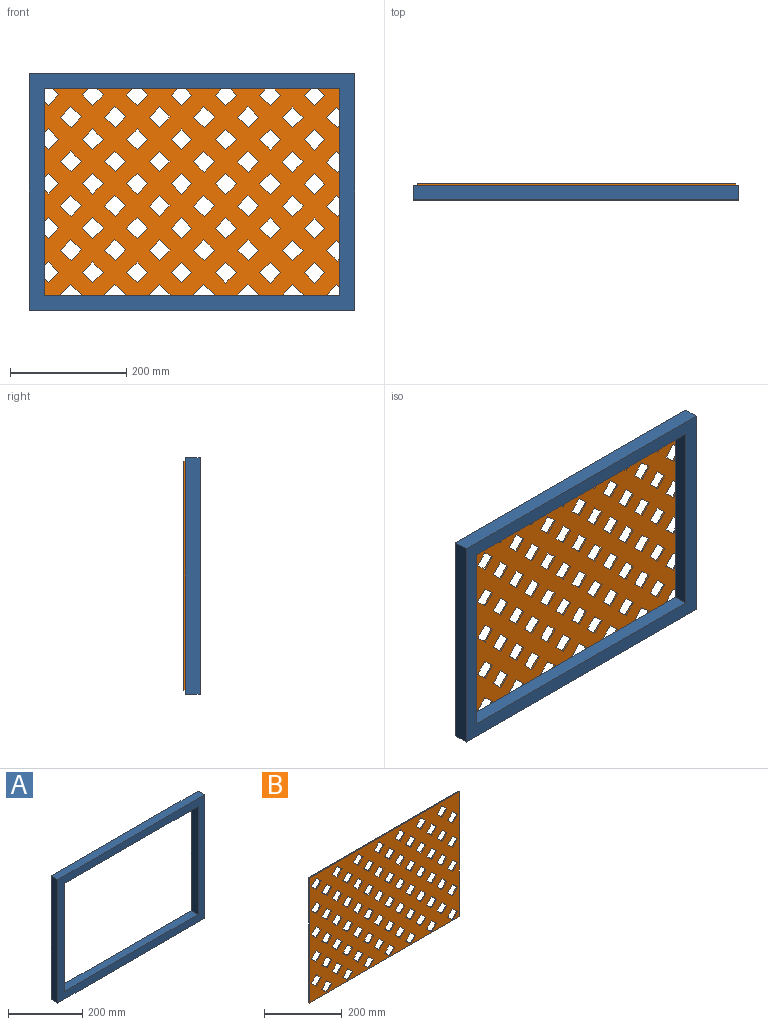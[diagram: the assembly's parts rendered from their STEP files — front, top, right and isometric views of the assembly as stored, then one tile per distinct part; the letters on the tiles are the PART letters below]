
ASSEMBLY  parts=2 mates=1
PART A: 10 faces, bbox 558.8x25.4x406.4 mm
  f0: plane 558.8x406.4mm, normal (0,-1,0), area 46451.5mm2, adj f2,f3,f4,f5,f6,f7,f8,f9
  f1: plane 558.8x406.4mm, normal (0,1,0), area 46451.5mm2, adj f2,f3,f4,f5,f6,f7,f8,f9
  f2: plane 558.8x25.4mm, normal (0,0,-1), area 14193.5mm2, adj f0,f1,f3,f5
  f3: plane 406.4x25.4mm, normal (1,0,0), area 10322.6mm2, adj f0,f1,f2,f4
  f4: plane 558.8x25.4mm, normal (0,0,1), area 14193.5mm2, adj f0,f1,f3,f5
  f5: plane 406.4x25.4mm, normal (-1,0,0), area 10322.6mm2, adj f0,f1,f2,f4
  f6: plane 508x25.4mm, normal (0,0,1), area 12903.2mm2, adj f0,f1,f7,f9
  f7: plane 355.6x25.4mm, normal (-1,0,0), area 9032.2mm2, adj f0,f1,f6,f8
  f8: plane 508x25.4mm, normal (0,0,-1), area 12903.2mm2, adj f0,f1,f7,f9
  f9: plane 355.6x25.4mm, normal (1,0,0), area 9032.2mm2, adj f0,f1,f6,f8
PART B: 286 faces, bbox 546.1x2.5x393.7 mm
  f0: plane 546.1x393.7mm, normal (0,-1,0), area 169838.4mm2, adj f2,f3,f4,f5,f6,f7,f8,f9
  f1: plane 546.1x393.7mm, normal (0,1,0), area 169838.4mm2, adj f2,f3,f4,f5,f6,f7,f8,f9
  f2: plane 546.1x2.54mm, normal (0,0,-1), area 1387.1mm2, adj f0,f1,f3,f5
  f3: plane 393.7x2.54mm, normal (1,0,0), area 1000mm2, adj f0,f1,f2,f4
  f4: plane 546.1x2.54mm, normal (0,0,1), area 1387.1mm2, adj f0,f1,f3,f5
  f5: plane 393.7x2.54mm, normal (-1,0,0), area 1000mm2, adj f0,f1,f2,f4
  f6: plane 17.96x17.96mm, normal (-0.71,0,-0.71), area 64.5mm2, adj f0,f1,f7,f8
  f7: plane 17.96x17.96mm, normal (-0.71,0,0.71), area 64.5mm2, adj f0,f1,f6,f9
  f8: plane 17.96x17.96mm, normal (0.71,0,-0.71), area 64.5mm2, adj f0,f1,f6,f9
  f9: plane 17.96x17.96mm, normal (0.71,0,0.71), area 64.5mm2, adj f0,f1,f7,f8
  f10: plane 17.96x17.96mm, normal (-0.71,0,-0.71), area 64.5mm2, adj f0,f1,f11,f12
  f11: plane 17.96x17.96mm, normal (-0.71,0,0.71), area 64.5mm2, adj f0,f1,f10,f13
  f12: plane 17.96x17.96mm, normal (0.71,0,-0.71), area 64.5mm2, adj f0,f1,f10,f13
  f13: plane 17.96x17.96mm, normal (0.71,0,0.71), area 64.5mm2, adj f0,f1,f11,f12
  f14: plane 18.43x17.48mm, normal (-0.69,0,-0.73), area 64.5mm2, adj f0,f1,f15,f16
  f15: plane 18.43x17.48mm, normal (-0.73,0,0.69), area 64.5mm2, adj f0,f1,f14,f17
  f16: plane 18.43x17.48mm, normal (0.73,0,-0.69), area 64.5mm2, adj f0,f1,f14,f17
  f17: plane 18.43x17.48mm, normal (0.69,0,0.73), area 64.5mm2, adj f0,f1,f15,f16
  f18: plane 18.43x17.48mm, normal (-0.69,0,-0.73), area 64.5mm2, adj f0,f1,f19,f20
  f19: plane 18.43x17.48mm, normal (-0.73,0,0.69), area 64.5mm2, adj f0,f1,f18,f21
  f20: plane 18.43x17.48mm, normal (0.73,0,-0.69), area 64.5mm2, adj f0,f1,f18,f21
  f21: plane 18.43x17.48mm, normal (0.69,0,0.73), area 64.5mm2, adj f0,f1,f19,f20
  f22: plane 17.96x17.96mm, normal (0.71,0,-0.71), area 64.5mm2, adj f0,f1,f23,f24
  f23: plane 17.96x17.96mm, normal (-0.71,0,-0.71), area 64.5mm2, adj f0,f1,f22,f25
  f24: plane 17.96x17.96mm, normal (0.71,0,0.71), area 64.5mm2, adj f0,f1,f22,f25
  f25: plane 17.96x17.96mm, normal (-0.71,0,0.71), area 64.5mm2, adj f0,f1,f23,f24
  f26: plane 18.43x17.48mm, normal (-0.69,0,-0.73), area 64.5mm2, adj f0,f1,f27,f28
  f27: plane 18.43x17.48mm, normal (-0.73,0,0.69), area 64.5mm2, adj f0,f1,f26,f29
  f28: plane 18.43x17.48mm, normal (0.73,0,-0.69), area 64.5mm2, adj f0,f1,f26,f29
  f29: plane 18.43x17.48mm, normal (0.69,0,0.73), area 64.5mm2, adj f0,f1,f27,f28
  f30: plane 17.96x17.96mm, normal (0.71,0,0.71), area 64.5mm2, adj f0,f1,f31,f33
  f31: plane 17.96x17.96mm, normal (-0.71,0,0.71), area 64.5mm2, adj f0,f1,f30,f32
  f32: plane 17.96x17.96mm, normal (-0.71,0,-0.71), area 64.5mm2, adj f0,f1,f31,f33
  f33: plane 17.96x17.96mm, normal (0.71,0,-0.71), area 64.5mm2, adj f0,f1,f30,f32
  f34: plane 17.96x17.96mm, normal (0.71,0,-0.71), area 64.5mm2, adj f0,f1,f35,f36
  f35: plane 17.96x17.96mm, normal (-0.71,0,-0.71), area 64.5mm2, adj f0,f1,f34,f37
  f36: plane 17.96x17.96mm, normal (0.71,0,0.71), area 64.5mm2, adj f0,f1,f34,f37
  f37: plane 17.96x17.96mm, normal (-0.71,0,0.71), area 64.5mm2, adj f0,f1,f35,f36
  f38: plane 17.96x17.96mm, normal (-0.71,0,-0.71), area 64.5mm2, adj f0,f1,f39,f40
  f39: plane 17.96x17.96mm, normal (-0.71,0,0.71), area 64.5mm2, adj f0,f1,f38,f41
  f40: plane 17.96x17.96mm, normal (0.71,0,-0.71), area 64.5mm2, adj f0,f1,f38,f41
  f41: plane 17.96x17.96mm, normal (0.71,0,0.71), area 64.5mm2, adj f0,f1,f39,f40
  f42: plane 18.43x17.48mm, normal (0.73,0,-0.69), area 64.5mm2, adj f0,f1,f43,f44
  f43: plane 18.43x17.48mm, normal (-0.69,0,-0.73), area 64.5mm2, adj f0,f1,f42,f45
  f44: plane 18.43x17.48mm, normal (0.69,0,0.73), area 64.5mm2, adj f0,f1,f42,f45
  f45: plane 18.43x17.48mm, normal (-0.73,0,0.69), area 64.5mm2, adj f0,f1,f43,f44
  f46: plane 18.43x17.48mm, normal (0.73,0,-0.69), area 64.5mm2, adj f0,f1,f47,f48
  f47: plane 18.43x17.48mm, normal (-0.69,0,-0.73), area 64.5mm2, adj f0,f1,f46,f49
  f48: plane 18.43x17.48mm, normal (0.69,0,0.73), area 64.5mm2, adj f0,f1,f46,f49
  f49: plane 18.43x17.48mm, normal (-0.73,0,0.69), area 64.5mm2, adj f0,f1,f47,f48
  f50: plane 18.43x17.48mm, normal (-0.69,0,-0.73), area 64.5mm2, adj f0,f1,f51,f52
  f51: plane 18.43x17.48mm, normal (-0.73,0,0.69), area 64.5mm2, adj f0,f1,f50,f53
  f52: plane 18.43x17.48mm, normal (0.73,0,-0.69), area 64.5mm2, adj f0,f1,f50,f53
  f53: plane 18.43x17.48mm, normal (0.69,0,0.73), area 64.5mm2, adj f0,f1,f51,f52
  f54: plane 17.96x17.96mm, normal (-0.71,0,-0.71), area 64.5mm2, adj f0,f1,f55,f56
  f55: plane 17.96x17.96mm, normal (-0.71,0,0.71), area 64.5mm2, adj f0,f1,f54,f57
  f56: plane 17.96x17.96mm, normal (0.71,0,-0.71), area 64.5mm2, adj f0,f1,f54,f57
  f57: plane 17.96x17.96mm, normal (0.71,0,0.71), area 64.5mm2, adj f0,f1,f55,f56
  f58: plane 18.43x17.48mm, normal (-0.69,0,-0.73), area 64.5mm2, adj f0,f1,f59,f60
  f59: plane 18.43x17.48mm, normal (-0.73,0,0.69), area 64.5mm2, adj f0,f1,f58,f61
  f60: plane 18.43x17.48mm, normal (0.73,0,-0.69), area 64.5mm2, adj f0,f1,f58,f61
  f61: plane 18.43x17.48mm, normal (0.69,0,0.73), area 64.5mm2, adj f0,f1,f59,f60
  f62: plane 18.43x17.48mm, normal (-0.69,0,-0.73), area 64.5mm2, adj f0,f1,f63,f64
  f63: plane 18.43x17.48mm, normal (-0.73,0,0.69), area 64.5mm2, adj f0,f1,f62,f65
  f64: plane 18.43x17.48mm, normal (0.73,0,-0.69), area 64.5mm2, adj f0,f1,f62,f65
  f65: plane 18.43x17.48mm, normal (0.69,0,0.73), area 64.5mm2, adj f0,f1,f63,f64
  f66: plane 18.43x17.48mm, normal (0.73,0,-0.69), area 64.5mm2, adj f0,f1,f67,f68
  f67: plane 18.43x17.48mm, normal (-0.69,0,-0.73), area 64.5mm2, adj f0,f1,f66,f69
  f68: plane 18.43x17.48mm, normal (0.69,0,0.73), area 64.5mm2, adj f0,f1,f66,f69
  f69: plane 18.43x17.48mm, normal (-0.73,0,0.69), area 64.5mm2, adj f0,f1,f67,f68
  f70: plane 17.96x17.96mm, normal (0.71,0,0.71), area 64.5mm2, adj f0,f1,f71,f73
  f71: plane 17.96x17.96mm, normal (-0.71,0,0.71), area 64.5mm2, adj f0,f1,f70,f72
  f72: plane 17.96x17.96mm, normal (-0.71,0,-0.71), area 64.5mm2, adj f0,f1,f71,f73
  f73: plane 17.96x17.96mm, normal (0.71,0,-0.71), area 64.5mm2, adj f0,f1,f70,f72
  f74: plane 17.96x17.96mm, normal (0.71,0,-0.71), area 64.5mm2, adj f0,f1,f75,f76
  f75: plane 17.96x17.96mm, normal (-0.71,0,-0.71), area 64.5mm2, adj f0,f1,f74,f77
  f76: plane 17.96x17.96mm, normal (0.71,0,0.71), area 64.5mm2, adj f0,f1,f74,f77
  f77: plane 17.96x17.96mm, normal (-0.71,0,0.71), area 64.5mm2, adj f0,f1,f75,f76
  f78: plane 17.96x17.96mm, normal (0.71,0,-0.71), area 64.5mm2, adj f0,f1,f79,f80
  f79: plane 17.96x17.96mm, normal (-0.71,0,-0.71), area 64.5mm2, adj f0,f1,f78,f81
  f80: plane 17.96x17.96mm, normal (0.71,0,0.71), area 64.5mm2, adj f0,f1,f78,f81
  f81: plane 17.96x17.96mm, normal (-0.71,0,0.71), area 64.5mm2, adj f0,f1,f79,f80
  f82: plane 18.43x17.48mm, normal (-0.69,0,-0.73), area 64.5mm2, adj f0,f1,f83,f84
  f83: plane 18.43x17.48mm, normal (-0.73,0,0.69), area 64.5mm2, adj f0,f1,f82,f85
  f84: plane 18.43x17.48mm, normal (0.73,0,-0.69), area 64.5mm2, adj f0,f1,f82,f85
  f85: plane 18.43x17.48mm, normal (0.69,0,0.73), area 64.5mm2, adj f0,f1,f83,f84
  f86: plane 18.43x17.48mm, normal (-0.69,0,-0.73), area 64.5mm2, adj f0,f1,f87,f88
  f87: plane 18.43x17.48mm, normal (-0.73,0,0.69), area 64.5mm2, adj f0,f1,f86,f89
  f88: plane 18.43x17.48mm, normal (0.73,0,-0.69), area 64.5mm2, adj f0,f1,f86,f89
  f89: plane 18.43x17.48mm, normal (0.69,0,0.73), area 64.5mm2, adj f0,f1,f87,f88
  f90: plane 17.96x17.96mm, normal (-0.71,0,-0.71), area 64.5mm2, adj f0,f1,f91,f92
  f91: plane 17.96x17.96mm, normal (-0.71,0,0.71), area 64.5mm2, adj f0,f1,f90,f93
  f92: plane 17.96x17.96mm, normal (0.71,0,-0.71), area 64.5mm2, adj f0,f1,f90,f93
  f93: plane 17.96x17.96mm, normal (0.71,0,0.71), area 64.5mm2, adj f0,f1,f91,f92
  f94: plane 17.96x17.96mm, normal (0.71,0,0.71), area 64.5mm2, adj f0,f1,f95,f97
  f95: plane 17.96x17.96mm, normal (-0.71,0,0.71), area 64.5mm2, adj f0,f1,f94,f96
  f96: plane 17.96x17.96mm, normal (-0.71,0,-0.71), area 64.5mm2, adj f0,f1,f95,f97
  f97: plane 17.96x17.96mm, normal (0.71,0,-0.71), area 64.5mm2, adj f0,f1,f94,f96
  f98: plane 18.43x17.48mm, normal (-0.69,0,-0.73), area 64.5mm2, adj f0,f1,f99,f100
  f99: plane 18.43x17.48mm, normal (-0.73,0,0.69), area 64.5mm2, adj f0,f1,f98,f101
  f100: plane 18.43x17.48mm, normal (0.73,0,-0.69), area 64.5mm2, adj f0,f1,f98,f101
  f101: plane 18.43x17.48mm, normal (0.69,0,0.73), area 64.5mm2, adj f0,f1,f99,f100
  f102: plane 17.96x17.96mm, normal (0.71,0,0.71), area 64.5mm2, adj f0,f1,f103,f105
  f103: plane 17.96x17.96mm, normal (-0.71,0,0.71), area 64.5mm2, adj f0,f1,f102,f104
  f104: plane 17.96x17.96mm, normal (-0.71,0,-0.71), area 64.5mm2, adj f0,f1,f103,f105
  f105: plane 17.96x17.96mm, normal (0.71,0,-0.71), area 64.5mm2, adj f0,f1,f102,f104
  f106: plane 18.43x17.48mm, normal (-0.69,0,-0.73), area 64.5mm2, adj f0,f1,f107,f108
  f107: plane 18.43x17.48mm, normal (-0.73,0,0.69), area 64.5mm2, adj f0,f1,f106,f109
  f108: plane 18.43x17.48mm, normal (0.73,0,-0.69), area 64.5mm2, adj f0,f1,f106,f109
  f109: plane 18.43x17.48mm, normal (0.69,0,0.73), area 64.5mm2, adj f0,f1,f107,f108
  f110: plane 18.43x17.48mm, normal (-0.69,0,-0.73), area 64.5mm2, adj f0,f1,f111,f112
  f111: plane 18.43x17.48mm, normal (-0.73,0,0.69), area 64.5mm2, adj f0,f1,f110,f113
  f112: plane 18.43x17.48mm, normal (0.73,0,-0.69), area 64.5mm2, adj f0,f1,f110,f113
  f113: plane 18.43x17.48mm, normal (0.69,0,0.73), area 64.5mm2, adj f0,f1,f111,f112
  f114: plane 18.43x17.48mm, normal (-0.69,0,-0.73), area 64.5mm2, adj f0,f1,f115,f116
  f115: plane 18.43x17.48mm, normal (-0.73,0,0.69), area 64.5mm2, adj f0,f1,f114,f117
  f116: plane 18.43x17.48mm, normal (0.73,0,-0.69), area 64.5mm2, adj f0,f1,f114,f117
  f117: plane 18.43x17.48mm, normal (0.69,0,0.73), area 64.5mm2, adj f0,f1,f115,f116
  f118: plane 17.96x17.96mm, normal (0.71,0,0.71), area 64.5mm2, adj f0,f1,f119,f121
  f119: plane 17.96x17.96mm, normal (-0.71,0,0.71), area 64.5mm2, adj f0,f1,f118,f120
  f120: plane 17.96x17.96mm, normal (-0.71,0,-0.71), area 64.5mm2, adj f0,f1,f119,f121
  f121: plane 17.96x17.96mm, normal (0.71,0,-0.71), area 64.5mm2, adj f0,f1,f118,f120
  f122: plane 18.43x17.48mm, normal (-0.69,0,-0.73), area 64.5mm2, adj f0,f1,f123,f124
  f123: plane 18.43x17.48mm, normal (-0.73,0,0.69), area 64.5mm2, adj f0,f1,f122,f125
  f124: plane 18.43x17.48mm, normal (0.73,0,-0.69), area 64.5mm2, adj f0,f1,f122,f125
  f125: plane 18.43x17.48mm, normal (0.69,0,0.73), area 64.5mm2, adj f0,f1,f123,f124
  f126: plane 17.96x17.96mm, normal (-0.71,0,-0.71), area 64.5mm2, adj f0,f1,f127,f128
  f127: plane 17.96x17.96mm, normal (-0.71,0,0.71), area 64.5mm2, adj f0,f1,f126,f129
  f128: plane 17.96x17.96mm, normal (0.71,0,-0.71), area 64.5mm2, adj f0,f1,f126,f129
  f129: plane 17.96x17.96mm, normal (0.71,0,0.71), area 64.5mm2, adj f0,f1,f127,f128
  f130: plane 18.43x17.48mm, normal (0.73,0,-0.69), area 64.5mm2, adj f0,f1,f131,f132
  f131: plane 18.43x17.48mm, normal (-0.69,0,-0.73), area 64.5mm2, adj f0,f1,f130,f133
  f132: plane 18.43x17.48mm, normal (0.69,0,0.73), area 64.5mm2, adj f0,f1,f130,f133
  f133: plane 18.43x17.48mm, normal (-0.73,0,0.69), area 64.5mm2, adj f0,f1,f131,f132
  f134: plane 17.96x17.96mm, normal (0.71,0,-0.71), area 64.5mm2, adj f0,f1,f135,f136
  f135: plane 17.96x17.96mm, normal (-0.71,0,-0.71), area 64.5mm2, adj f0,f1,f134,f137
  f136: plane 17.96x17.96mm, normal (0.71,0,0.71), area 64.5mm2, adj f0,f1,f134,f137
  f137: plane 17.96x17.96mm, normal (-0.71,0,0.71), area 64.5mm2, adj f0,f1,f135,f136
  f138: plane 18.43x17.48mm, normal (-0.69,0,-0.73), area 64.5mm2, adj f0,f1,f139,f140
  f139: plane 18.43x17.48mm, normal (-0.73,0,0.69), area 64.5mm2, adj f0,f1,f138,f141
  f140: plane 18.43x17.48mm, normal (0.73,0,-0.69), area 64.5mm2, adj f0,f1,f138,f141
  f141: plane 18.43x17.48mm, normal (0.69,0,0.73), area 64.5mm2, adj f0,f1,f139,f140
  f142: plane 17.96x17.96mm, normal (0.71,0,0.71), area 64.5mm2, adj f0,f1,f143,f145
  f143: plane 17.96x17.96mm, normal (-0.71,0,0.71), area 64.5mm2, adj f0,f1,f142,f144
  f144: plane 17.96x17.96mm, normal (-0.71,0,-0.71), area 64.5mm2, adj f0,f1,f143,f145
  f145: plane 17.96x17.96mm, normal (0.71,0,-0.71), area 64.5mm2, adj f0,f1,f142,f144
  f146: plane 18.43x17.48mm, normal (0.73,0,-0.69), area 64.5mm2, adj f0,f1,f147,f148
  f147: plane 18.43x17.48mm, normal (-0.69,0,-0.73), area 64.5mm2, adj f0,f1,f146,f149
  f148: plane 18.43x17.48mm, normal (0.69,0,0.73), area 64.5mm2, adj f0,f1,f146,f149
  f149: plane 18.43x17.48mm, normal (-0.73,0,0.69), area 64.5mm2, adj f0,f1,f147,f148
  f150: plane 17.96x17.96mm, normal (0.71,0,0.71), area 64.5mm2, adj f0,f1,f151,f153
  f151: plane 17.96x17.96mm, normal (-0.71,0,0.71), area 64.5mm2, adj f0,f1,f150,f152
  f152: plane 17.96x17.96mm, normal (-0.71,0,-0.71), area 64.5mm2, adj f0,f1,f151,f153
  f153: plane 17.96x17.96mm, normal (0.71,0,-0.71), area 64.5mm2, adj f0,f1,f150,f152
  f154: plane 17.96x17.96mm, normal (0.71,0,-0.71), area 64.5mm2, adj f0,f1,f155,f156
  f155: plane 17.96x17.96mm, normal (-0.71,0,-0.71), area 64.5mm2, adj f0,f1,f154,f157
  f156: plane 17.96x17.96mm, normal (0.71,0,0.71), area 64.5mm2, adj f0,f1,f154,f157
  f157: plane 17.96x17.96mm, normal (-0.71,0,0.71), area 64.5mm2, adj f0,f1,f155,f156
  f158: plane 17.96x17.96mm, normal (-0.71,0,-0.71), area 64.5mm2, adj f0,f1,f159,f160
  f159: plane 17.96x17.96mm, normal (-0.71,0,0.71), area 64.5mm2, adj f0,f1,f158,f161
  f160: plane 17.96x17.96mm, normal (0.71,0,-0.71), area 64.5mm2, adj f0,f1,f158,f161
  f161: plane 17.96x17.96mm, normal (0.71,0,0.71), area 64.5mm2, adj f0,f1,f159,f160
  f162: plane 18.43x17.48mm, normal (0.73,0,-0.69), area 64.5mm2, adj f0,f1,f163,f164
  f163: plane 18.43x17.48mm, normal (-0.69,0,-0.73), area 64.5mm2, adj f0,f1,f162,f165
  f164: plane 18.43x17.48mm, normal (0.69,0,0.73), area 64.5mm2, adj f0,f1,f162,f165
  f165: plane 18.43x17.48mm, normal (-0.73,0,0.69), area 64.5mm2, adj f0,f1,f163,f164
  f166: plane 17.96x17.96mm, normal (0.71,0,-0.71), area 64.5mm2, adj f0,f1,f167,f168
  f167: plane 17.96x17.96mm, normal (-0.71,0,-0.71), area 64.5mm2, adj f0,f1,f166,f169
  f168: plane 17.96x17.96mm, normal (0.71,0,0.71), area 64.5mm2, adj f0,f1,f166,f169
  f169: plane 17.96x17.96mm, normal (-0.71,0,0.71), area 64.5mm2, adj f0,f1,f167,f168
  f170: plane 18.43x17.48mm, normal (-0.69,0,-0.73), area 64.5mm2, adj f0,f1,f171,f172
  f171: plane 18.43x17.48mm, normal (-0.73,0,0.69), area 64.5mm2, adj f0,f1,f170,f173
  f172: plane 18.43x17.48mm, normal (0.73,0,-0.69), area 64.5mm2, adj f0,f1,f170,f173
  f173: plane 18.43x17.48mm, normal (0.69,0,0.73), area 64.5mm2, adj f0,f1,f171,f172
  f174: plane 18.43x17.48mm, normal (-0.69,0,-0.73), area 64.5mm2, adj f0,f1,f175,f176
  f175: plane 18.43x17.48mm, normal (-0.73,0,0.69), area 64.5mm2, adj f0,f1,f174,f177
  f176: plane 18.43x17.48mm, normal (0.73,0,-0.69), area 64.5mm2, adj f0,f1,f174,f177
  f177: plane 18.43x17.48mm, normal (0.69,0,0.73), area 64.5mm2, adj f0,f1,f175,f176
  f178: plane 18.43x17.48mm, normal (0.73,0,-0.69), area 64.5mm2, adj f0,f1,f179,f180
  f179: plane 18.43x17.48mm, normal (-0.69,0,-0.73), area 64.5mm2, adj f0,f1,f178,f181
  f180: plane 18.43x17.48mm, normal (0.69,0,0.73), area 64.5mm2, adj f0,f1,f178,f181
  f181: plane 18.43x17.48mm, normal (-0.73,0,0.69), area 64.5mm2, adj f0,f1,f179,f180
  f182: plane 17.96x17.96mm, normal (0.71,0,0.71), area 64.5mm2, adj f0,f1,f183,f185
  f183: plane 17.96x17.96mm, normal (-0.71,0,0.71), area 64.5mm2, adj f0,f1,f182,f184
  f184: plane 17.96x17.96mm, normal (-0.71,0,-0.71), area 64.5mm2, adj f0,f1,f183,f185
  f185: plane 17.96x17.96mm, normal (0.71,0,-0.71), area 64.5mm2, adj f0,f1,f182,f184
  f186: plane 17.96x17.96mm, normal (0.71,0,-0.71), area 64.5mm2, adj f0,f1,f187,f188
  f187: plane 17.96x17.96mm, normal (-0.71,0,-0.71), area 64.5mm2, adj f0,f1,f186,f189
  f188: plane 17.96x17.96mm, normal (0.71,0,0.71), area 64.5mm2, adj f0,f1,f186,f189
  f189: plane 17.96x17.96mm, normal (-0.71,0,0.71), area 64.5mm2, adj f0,f1,f187,f188
  f190: plane 17.96x17.96mm, normal (0.71,0,0.71), area 64.5mm2, adj f0,f1,f191,f193
  f191: plane 17.96x17.96mm, normal (-0.71,0,0.71), area 64.5mm2, adj f0,f1,f190,f192
  f192: plane 17.96x17.96mm, normal (-0.71,0,-0.71), area 64.5mm2, adj f0,f1,f191,f193
  f193: plane 17.96x17.96mm, normal (0.71,0,-0.71), area 64.5mm2, adj f0,f1,f190,f192
  f194: plane 17.96x17.96mm, normal (0.71,0,-0.71), area 64.5mm2, adj f0,f1,f195,f196
  f195: plane 17.96x17.96mm, normal (-0.71,0,-0.71), area 64.5mm2, adj f0,f1,f194,f197
  f196: plane 17.96x17.96mm, normal (0.71,0,0.71), area 64.5mm2, adj f0,f1,f194,f197
  f197: plane 17.96x17.96mm, normal (-0.71,0,0.71), area 64.5mm2, adj f0,f1,f195,f196
  f198: plane 17.96x17.96mm, normal (-0.71,0,-0.71), area 64.5mm2, adj f0,f1,f199,f200
  f199: plane 17.96x17.96mm, normal (-0.71,0,0.71), area 64.5mm2, adj f0,f1,f198,f201
  f200: plane 17.96x17.96mm, normal (0.71,0,-0.71), area 64.5mm2, adj f0,f1,f198,f201
  f201: plane 17.96x17.96mm, normal (0.71,0,0.71), area 64.5mm2, adj f0,f1,f199,f200
  f202: plane 18.43x17.48mm, normal (0.73,0,-0.69), area 64.5mm2, adj f0,f1,f203,f204
  f203: plane 18.43x17.48mm, normal (-0.69,0,-0.73), area 64.5mm2, adj f0,f1,f202,f205
  f204: plane 18.43x17.48mm, normal (0.69,0,0.73), area 64.5mm2, adj f0,f1,f202,f205
  f205: plane 18.43x17.48mm, normal (-0.73,0,0.69), area 64.5mm2, adj f0,f1,f203,f204
  f206: plane 18.43x17.48mm, normal (0.73,0,-0.69), area 64.5mm2, adj f0,f1,f207,f208
  f207: plane 18.43x17.48mm, normal (-0.69,0,-0.73), area 64.5mm2, adj f0,f1,f206,f209
  f208: plane 18.43x17.48mm, normal (0.69,0,0.73), area 64.5mm2, adj f0,f1,f206,f209
  f209: plane 18.43x17.48mm, normal (-0.73,0,0.69), area 64.5mm2, adj f0,f1,f207,f208
  f210: plane 18.43x17.48mm, normal (-0.69,0,-0.73), area 64.5mm2, adj f0,f1,f211,f212
  f211: plane 18.43x17.48mm, normal (-0.73,0,0.69), area 64.5mm2, adj f0,f1,f210,f213
  f212: plane 18.43x17.48mm, normal (0.73,0,-0.69), area 64.5mm2, adj f0,f1,f210,f213
  f213: plane 18.43x17.48mm, normal (0.69,0,0.73), area 64.5mm2, adj f0,f1,f211,f212
  f214: plane 17.96x17.96mm, normal (-0.71,0,-0.71), area 64.5mm2, adj f0,f1,f215,f216
  f215: plane 17.96x17.96mm, normal (-0.71,0,0.71), area 64.5mm2, adj f0,f1,f214,f217
  f216: plane 17.96x17.96mm, normal (0.71,0,-0.71), area 64.5mm2, adj f0,f1,f214,f217
  f217: plane 17.96x17.96mm, normal (0.71,0,0.71), area 64.5mm2, adj f0,f1,f215,f216
  f218: plane 18.43x17.48mm, normal (-0.69,0,-0.73), area 64.5mm2, adj f0,f1,f219,f220
  f219: plane 18.43x17.48mm, normal (-0.73,0,0.69), area 64.5mm2, adj f0,f1,f218,f221
  f220: plane 18.43x17.48mm, normal (0.73,0,-0.69), area 64.5mm2, adj f0,f1,f218,f221
  f221: plane 18.43x17.48mm, normal (0.69,0,0.73), area 64.5mm2, adj f0,f1,f219,f220
  f222: plane 18.43x17.48mm, normal (0.73,0,-0.69), area 64.5mm2, adj f0,f1,f223,f224
  f223: plane 18.43x17.48mm, normal (-0.69,0,-0.73), area 64.5mm2, adj f0,f1,f222,f225
  f224: plane 18.43x17.48mm, normal (0.69,0,0.73), area 64.5mm2, adj f0,f1,f222,f225
  f225: plane 18.43x17.48mm, normal (-0.73,0,0.69), area 64.5mm2, adj f0,f1,f223,f224
  f226: plane 18.43x17.48mm, normal (-0.69,0,-0.73), area 64.5mm2, adj f0,f1,f227,f228
  f227: plane 18.43x17.48mm, normal (-0.73,0,0.69), area 64.5mm2, adj f0,f1,f226,f229
  f228: plane 18.43x17.48mm, normal (0.73,0,-0.69), area 64.5mm2, adj f0,f1,f226,f229
  f229: plane 18.43x17.48mm, normal (0.69,0,0.73), area 64.5mm2, adj f0,f1,f227,f228
  f230: plane 17.96x17.96mm, normal (-0.71,0,-0.71), area 64.5mm2, adj f0,f1,f231,f232
  f231: plane 17.96x17.96mm, normal (-0.71,0,0.71), area 64.5mm2, adj f0,f1,f230,f233
  f232: plane 17.96x17.96mm, normal (0.71,0,-0.71), area 64.5mm2, adj f0,f1,f230,f233
  f233: plane 17.96x17.96mm, normal (0.71,0,0.71), area 64.5mm2, adj f0,f1,f231,f232
  f234: plane 18.43x17.48mm, normal (-0.69,0,-0.73), area 64.5mm2, adj f0,f1,f235,f236
  f235: plane 18.43x17.48mm, normal (-0.73,0,0.69), area 64.5mm2, adj f0,f1,f234,f237
  f236: plane 18.43x17.48mm, normal (0.73,0,-0.69), area 64.5mm2, adj f0,f1,f234,f237
  f237: plane 18.43x17.48mm, normal (0.69,0,0.73), area 64.5mm2, adj f0,f1,f235,f236
  f238: plane 17.96x17.96mm, normal (-0.71,0,-0.71), area 64.5mm2, adj f0,f1,f239,f240
  f239: plane 17.96x17.96mm, normal (-0.71,0,0.71), area 64.5mm2, adj f0,f1,f238,f241
  f240: plane 17.96x17.96mm, normal (0.71,0,-0.71), area 64.5mm2, adj f0,f1,f238,f241
  f241: plane 17.96x17.96mm, normal (0.71,0,0.71), area 64.5mm2, adj f0,f1,f239,f240
  f242: plane 18.43x17.48mm, normal (0.73,0,-0.69), area 64.5mm2, adj f0,f1,f243,f244
  f243: plane 18.43x17.48mm, normal (-0.69,0,-0.73), area 64.5mm2, adj f0,f1,f242,f245
  f244: plane 18.43x17.48mm, normal (0.69,0,0.73), area 64.5mm2, adj f0,f1,f242,f245
  f245: plane 18.43x17.48mm, normal (-0.73,0,0.69), area 64.5mm2, adj f0,f1,f243,f244
  f246: plane 17.96x17.96mm, normal (0.71,0,-0.71), area 64.5mm2, adj f0,f1,f247,f248
  f247: plane 17.96x17.96mm, normal (-0.71,0,-0.71), area 64.5mm2, adj f0,f1,f246,f249
  f248: plane 17.96x17.96mm, normal (0.71,0,0.71), area 64.5mm2, adj f0,f1,f246,f249
  f249: plane 17.96x17.96mm, normal (-0.71,0,0.71), area 64.5mm2, adj f0,f1,f247,f248
  f250: plane 18.43x17.48mm, normal (-0.69,0,-0.73), area 64.5mm2, adj f0,f1,f251,f252
  f251: plane 18.43x17.48mm, normal (-0.73,0,0.69), area 64.5mm2, adj f0,f1,f250,f253
  f252: plane 18.43x17.48mm, normal (0.73,0,-0.69), area 64.5mm2, adj f0,f1,f250,f253
  f253: plane 18.43x17.48mm, normal (0.69,0,0.73), area 64.5mm2, adj f0,f1,f251,f252
  f254: plane 17.96x17.96mm, normal (0.71,0,-0.71), area 64.5mm2, adj f0,f1,f255,f256
  f255: plane 17.96x17.96mm, normal (-0.71,0,-0.71), area 64.5mm2, adj f0,f1,f254,f257
  f256: plane 17.96x17.96mm, normal (0.71,0,0.71), area 64.5mm2, adj f0,f1,f254,f257
  f257: plane 17.96x17.96mm, normal (-0.71,0,0.71), area 64.5mm2, adj f0,f1,f255,f256
  f258: plane 18.43x17.48mm, normal (-0.69,0,-0.73), area 64.5mm2, adj f0,f1,f259,f260
  f259: plane 18.43x17.48mm, normal (-0.73,0,0.69), area 64.5mm2, adj f0,f1,f258,f261
  f260: plane 18.43x17.48mm, normal (0.73,0,-0.69), area 64.5mm2, adj f0,f1,f258,f261
  f261: plane 18.43x17.48mm, normal (0.69,0,0.73), area 64.5mm2, adj f0,f1,f259,f260
  f262: plane 18.43x17.48mm, normal (-0.69,0,-0.73), area 64.5mm2, adj f0,f1,f263,f264
  f263: plane 18.43x17.48mm, normal (-0.73,0,0.69), area 64.5mm2, adj f0,f1,f262,f265
  f264: plane 18.43x17.48mm, normal (0.73,0,-0.69), area 64.5mm2, adj f0,f1,f262,f265
  f265: plane 18.43x17.48mm, normal (0.69,0,0.73), area 64.5mm2, adj f0,f1,f263,f264
  f266: plane 17.96x17.96mm, normal (-0.71,0,-0.71), area 64.5mm2, adj f0,f1,f267,f268
  f267: plane 17.96x17.96mm, normal (-0.71,0,0.71), area 64.5mm2, adj f0,f1,f266,f269
  f268: plane 17.96x17.96mm, normal (0.71,0,-0.71), area 64.5mm2, adj f0,f1,f266,f269
  f269: plane 17.96x17.96mm, normal (0.71,0,0.71), area 64.5mm2, adj f0,f1,f267,f268
  f270: plane 17.96x17.96mm, normal (0.71,0,0.71), area 64.5mm2, adj f0,f1,f271,f273
  f271: plane 17.96x17.96mm, normal (-0.71,0,0.71), area 64.5mm2, adj f0,f1,f270,f272
  f272: plane 17.96x17.96mm, normal (-0.71,0,-0.71), area 64.5mm2, adj f0,f1,f271,f273
  f273: plane 17.96x17.96mm, normal (0.71,0,-0.71), area 64.5mm2, adj f0,f1,f270,f272
  f274: plane 17.96x17.96mm, normal (0.71,0,-0.71), area 64.5mm2, adj f0,f1,f275,f276
  f275: plane 17.96x17.96mm, normal (-0.71,0,-0.71), area 64.5mm2, adj f0,f1,f274,f277
  f276: plane 17.96x17.96mm, normal (0.71,0,0.71), area 64.5mm2, adj f0,f1,f274,f277
  f277: plane 17.96x17.96mm, normal (-0.71,0,0.71), area 64.5mm2, adj f0,f1,f275,f276
  f278: plane 17.96x17.96mm, normal (-0.71,0,-0.71), area 64.5mm2, adj f0,f1,f279,f280
  f279: plane 17.96x17.96mm, normal (-0.71,0,0.71), area 64.5mm2, adj f0,f1,f278,f281
  f280: plane 17.96x17.96mm, normal (0.71,0,-0.71), area 64.5mm2, adj f0,f1,f278,f281
  f281: plane 17.96x17.96mm, normal (0.71,0,0.71), area 64.5mm2, adj f0,f1,f279,f280
  f282: plane 18.43x17.48mm, normal (0.73,0,-0.69), area 64.5mm2, adj f0,f1,f283,f284
  f283: plane 18.43x17.48mm, normal (-0.69,0,-0.73), area 64.5mm2, adj f0,f1,f282,f285
  f284: plane 18.43x17.48mm, normal (0.69,0,0.73), area 64.5mm2, adj f0,f1,f282,f285
  f285: plane 18.43x17.48mm, normal (-0.73,0,0.69), area 64.5mm2, adj f0,f1,f283,f284
PLACE A t=(-58.54,48.06,-39.54)mm
PLACE B t=(-57.59,50.6,-38.84)mm
MATE fastened A.f1 <-> B.f0  axis (0,1,0) through (199.27,48.06,-207.18)mm
